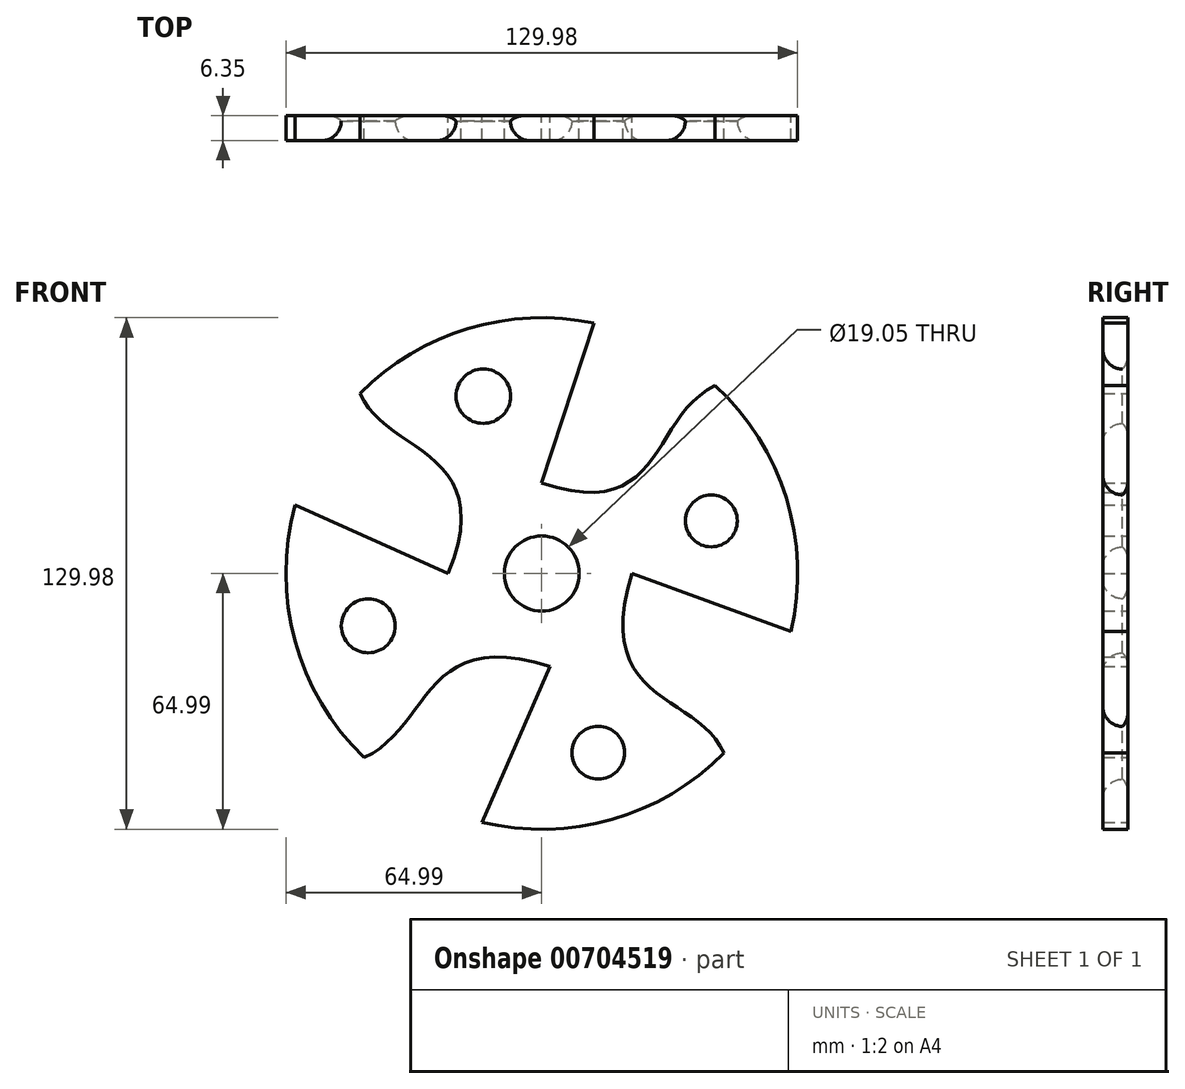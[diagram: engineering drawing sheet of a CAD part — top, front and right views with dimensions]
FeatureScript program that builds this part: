
annotation { "Feature Type Name" : "Feature", "Feature Type Description" : "" }
export const myFeature = defineFeature(function(context is Context, id is Id, definition is map)
    precondition{}
    {
        {
            var Q0;
            Q0=qCreatedBy(makeId("Front.planeOp"),FACE);
            var sketch = newSketch(context, id + "F0", { "sketchPlane" : qUnion([Q0])});
            skCircle(sketch, "E0", {"center": v(0, 0) * mm, "radius": 65 * mm});
            skCircle(sketch, "E1", {"center": v(0, 0) * mm, "radius": 20 * mm});
            skFitSpline(sketch, "E2", {"points": [v(-46.15, 45.76) * mm, v(-23.76, 0) * mm], "startDerivative": vector(19.5, -45.94) * mm, "endDerivative": vector(-38.85, -94.86) * mm});
            skLineSegment(sketch, "E3", {"start": v(-23.76, 0) * mm, "end": v(-62.63, 17.36) * mm});
            skFitSpline(sketch, "E4", {"points": [v(46.29, -45.62) * mm, v(22.86, 0) * mm], "startDerivative": vector(-19.44, 45.6) * mm, "endDerivative": vector(30.55, 100.19) * mm});
            skLineSegment(sketch, "E5", {"start": v(22.86, 0) * mm, "end": v(63.3, -14.7) * mm});
            skFitSpline(sketch, "E6", {"points": [v(-45.13, -46.77) * mm, v(2.1, -23.67) * mm], "startDerivative": vector(50.7, 22.86) * mm, "endDerivative": vector(97.39, -31.22) * mm});
            skLineSegment(sketch, "E7", {"start": v(2.1, -23.67) * mm, "end": v(-15.21, -63.19) * mm});
            skFitSpline(sketch, "E8", {"points": [v(44.03, 47.8) * mm, v(0, 22.95) * mm], "startDerivative": vector(-49.55, -24.61) * mm, "endDerivative": vector(-93.62, 31.22) * mm});
            skLineSegment(sketch, "E9", {"start": v(0, 22.95) * mm, "end": v(13.33, 63.61) * mm});
            skCircle(sketch, "E10", {"center": v(-44.08, -13.3) * mm, "radius": 12.59 * mm});
            skCircle(sketch, "E11", {"center": v(14.36, -45.54) * mm, "radius": 12.2 * mm});
            skCircle(sketch, "E12", {"center": v(43.08, 13.38) * mm, "radius": 12.64 * mm});
            skCircle(sketch, "E13", {"center": v(-14.85, 45.05) * mm, "radius": 12.68 * mm});
            skCircle(sketch, "E14", {"center": v(43.08, 13.38) * mm, "radius": 6.6 * mm});
            skCircle(sketch, "E15", {"center": v(14.36, -45.54) * mm, "radius": 6.7 * mm});
            skCircle(sketch, "E16", {"center": v(-44.08, -13.3) * mm, "radius": 6.86 * mm});
            skCircle(sketch, "E17", {"center": v(-14.85, 45.05) * mm, "radius": 6.91 * mm});
            skCircle(sketch, "E18", {"center": v(0, 0) * mm, "radius": 9.52 * mm});
            skSolve(sketch);
        }
        {
            var Q0;
            Q0=makeQuery(id+"F0.imprint","IMPRINT",FACE,{"disambiguationData":[TD([[makeQuery(id+"F0.imprint","IMPRINT",EDGE,{"derivedFrom":sQuery(id+"F0.wireOp",EDGE,"E1")}),-1.0]])]});
            var Q1;
            Q1=makeQuery(id+"F0.imprint","IMPRINT",FACE,{"disambiguationData":[TD([[makeQuery(id+"F0.imprint","IMPRINT",EDGE,{"derivedFrom":sQuery(id+"F0.wireOp",EDGE,"E1")}),1.0]])]});
            var Q2;
            Q2=makeQuery(id+"F0.imprint","IMPRINT",FACE,{"disambiguationData":[TD([[makeQuery(id+"F0.imprint","IMPRINT",EDGE,{"derivedFrom":sQuery(id+"F0.wireOp",EDGE,"E11")}),1.0]])]});
            var Q3;
            Q3=makeQuery(id+"F0.imprint","IMPRINT",FACE,{"disambiguationData":[TD([[makeQuery(id+"F0.imprint","IMPRINT",EDGE,{"derivedFrom":sQuery(id+"F0.wireOp",EDGE,"E12")}),1.0]])]});
            var Q4;
            Q4=makeQuery(id+"F0.imprint","IMPRINT",FACE,{"disambiguationData":[TD([[makeQuery(id+"F0.imprint","IMPRINT",EDGE,{"derivedFrom":sQuery(id+"F0.wireOp",EDGE,"E13")}),1.0]])]});
            var Q5;
            Q5=makeQuery(id+"F0.imprint","IMPRINT",FACE,{"disambiguationData":[TD([[makeQuery(id+"F0.imprint","IMPRINT",EDGE,{"derivedFrom":sQuery(id+"F0.wireOp",EDGE,"E10")}),1.0]])]});
            extrude(context, id + "F1", {"entities" : qUnion([Q0, Q1, Q2, Q3, Q4, Q5]), "depth" : 6.35 * mm, "offsetDistance" : 25.4 * mm});
        }
        {
            var Q0;
            Q0=makeQuery(id+"F1.opExtrude","CAP_EDGE",EDGE,{"disambiguationData":[OSD([sQuery(id+"F0.wireOp",EDGE,"E17")])],"isStart":false});
            fillet(context, id + "F2", {"entities" : qUnion([Q0]), "radius" : 5 * mm, "tangentPropagation" : true, "allowEdgeOverflow" : false});
        }
        {
            var Q0;
            Q0=makeQuery(id+"F1.opExtrude","CAP_EDGE",EDGE,{"disambiguationData":[OSD([sQuery(id+"F0.wireOp",EDGE,"E17")])],"isStart":true});
            fillet(context, id + "F3", {"entities" : qUnion([Q0]), "radius" : 5 * mm, "tangentPropagation" : true, "allowEdgeOverflow" : false});
        }
        {
            var Q0;
            Q0=makeQuery(id+"F1.opExtrude","CAP_EDGE",EDGE,{"disambiguationData":[OSD([sQuery(id+"F0.wireOp",EDGE,"E15")])],"isStart":false});
            fillet(context, id + "F4", {"entities" : qUnion([Q0]), "radius" : 5 * mm, "tangentPropagation" : true, "allowEdgeOverflow" : false});
        }
        {
            var Q0;
            Q0=makeQuery(id+"F1.opExtrude","CAP_EDGE",EDGE,{"disambiguationData":[OSD([sQuery(id+"F0.wireOp",EDGE,"E15")])],"isStart":true});
            fillet(context, id + "F5", {"entities" : qUnion([Q0]), "radius" : 5 * mm, "tangentPropagation" : true, "allowEdgeOverflow" : false});
        }
        {
            var Q0;
            Q0=makeQuery(id+"F1.opExtrude","CAP_EDGE",EDGE,{"disambiguationData":[OSD([sQuery(id+"F0.wireOp",EDGE,"E16")])],"isStart":false});
            fillet(context, id + "F6", {"entities" : qUnion([Q0]), "radius" : 5 * mm, "tangentPropagation" : true, "allowEdgeOverflow" : false});
        }
        {
            var Q0;
            Q0=makeQuery(id+"F1.opExtrude","CAP_EDGE",EDGE,{"disambiguationData":[OSD([sQuery(id+"F0.wireOp",EDGE,"E16")])],"isStart":true});
            fillet(context, id + "F7", {"entities" : qUnion([Q0]), "radius" : 5 * mm, "tangentPropagation" : true, "allowEdgeOverflow" : false});
        }
        {
            var Q0;
            Q0=makeQuery(id+"F1.opExtrude","CAP_EDGE",EDGE,{"disambiguationData":[OSD([sQuery(id+"F0.wireOp",EDGE,"E14")])],"isStart":false});
            fillet(context, id + "F8", {"entities" : qUnion([Q0]), "radius" : 5 * mm, "tangentPropagation" : true, "allowEdgeOverflow" : false});
        }
        {
            var Q0;
            Q0=makeQuery(id+"F1.opExtrude","CAP_EDGE",EDGE,{"disambiguationData":[OSD([sQuery(id+"F0.wireOp",EDGE,"E14")])],"isStart":true});
            fillet(context, id + "F9", {"entities" : qUnion([Q0]), "radius" : 5 * mm, "tangentPropagation" : true, "allowEdgeOverflow" : false});
        }
    });
